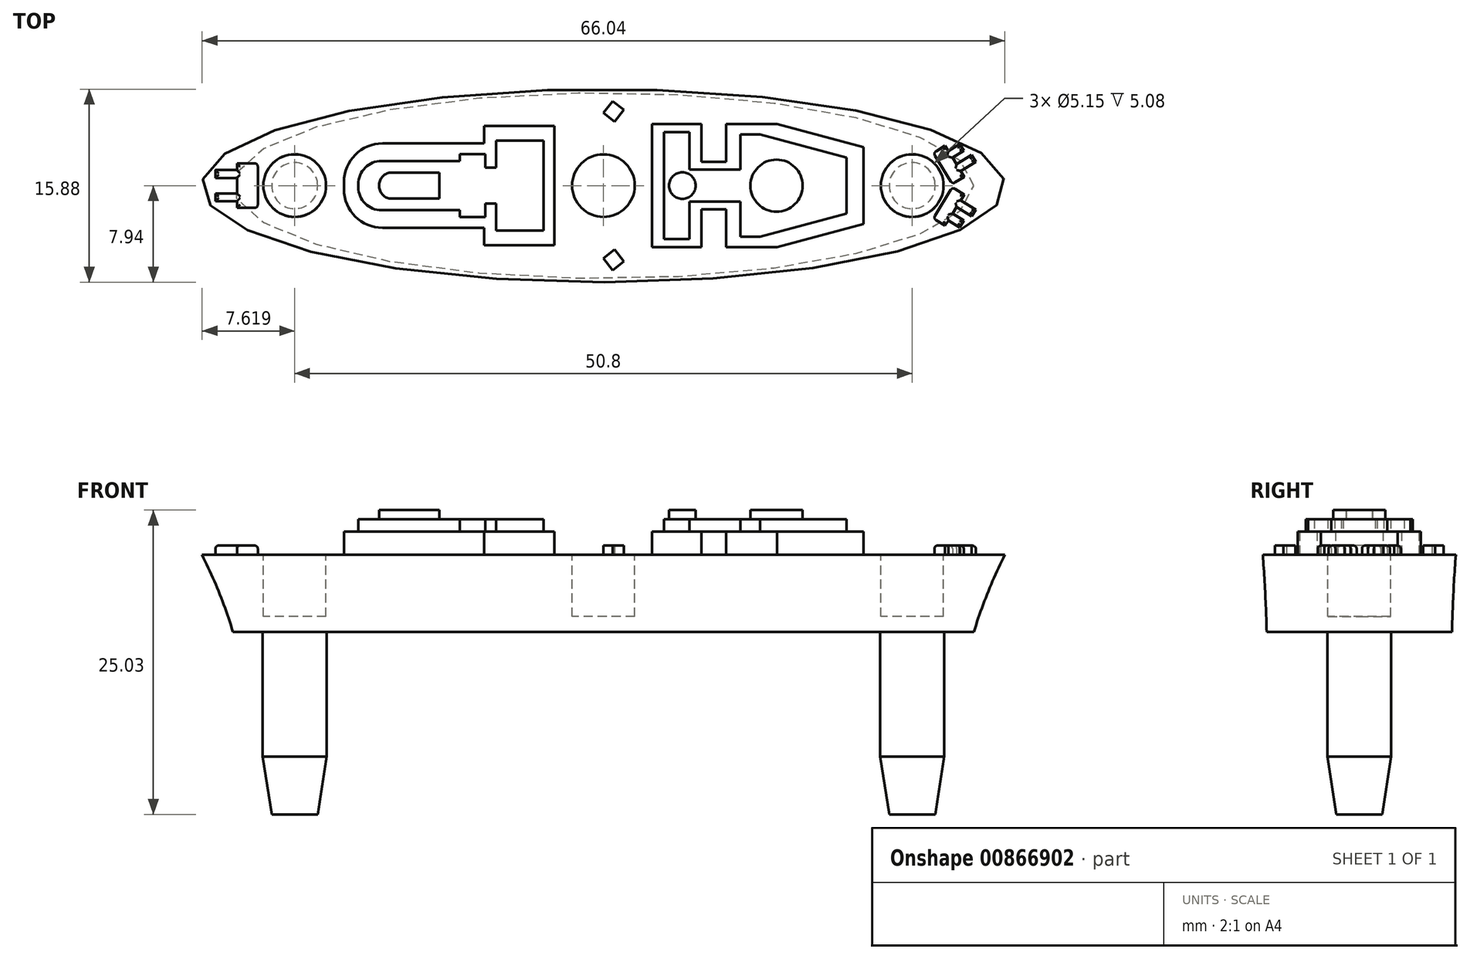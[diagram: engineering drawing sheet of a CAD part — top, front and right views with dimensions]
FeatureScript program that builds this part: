
annotation { "Feature Type Name" : "Feature", "Feature Type Description" : "" }
export const myFeature = defineFeature(function(context is Context, id is Id, definition is map)
    precondition{}
    {
        {
            var Q0;
            Q0=qCreatedBy(makeId("Top.planeOp"),FACE);
            var sketch = newSketch(context, id + "F0", { "sketchPlane" : qUnion([Q0])});
            skEllipse(sketch, "E0", {"center": v(0, 0) * mm, "majorRadius": 33.02 * mm, "minorRadius": 7.94 * mm, "majorAxis": v(1, 0)});
            skSolve(sketch);
        }
        {
            var Q0;
            Q0=qCreatedBy(makeId("Top.planeOp"),FACE);
            cPlane(context, id + "F1", {"entities" : qUnion([Q0]), "cplaneType" : CPlaneType.OFFSET, "offset" : 6.35 * mm, "oppositeDirection" : true, "width" : 152.4 * mm, "height" : 152.4 * mm});
        }
        {
            var Q0;
            Q0=qCreatedBy(id+"F1.planeOp",FACE);
            var sketch = newSketch(context, id + "F2", { "sketchPlane" : qUnion([Q0])});
            skEllipse(sketch, "E1", {"center": v(0, 0) * mm, "majorRadius": 30.48 * mm, "minorRadius": 7.62 * mm, "majorAxis": v(1, 0)});
            skSolve(sketch);
        }
        {
            var Q0;
            Q0=makeQuery(id+"F2.imprint","IMPRINT",FACE,{"disambiguationData":[TD([[makeQuery(id+"F2.imprint","IMPRINT",EDGE,{"derivedFrom":sQuery(id+"F2.wireOp",EDGE,"E1")}),1.0]])]});
            var Q1;
            Q1=makeQuery(id+"F0.imprint","IMPRINT",FACE,{"disambiguationData":[TD([[makeQuery(id+"F0.imprint","IMPRINT",EDGE,{"derivedFrom":sQuery(id+"F0.wireOp",EDGE,"E0")}),1.0]])]});
            loft(context, id + "F3", {"sheetProfilesArray" : [{ "sheetProfileEntities" : qUnion([Q0]) }, { "sheetProfileEntities" : qUnion([Q1]) }]});
        }
        {
            var Q0;
            Q0=qCreatedBy(id+"F1.planeOp",FACE);
            var sketch = newSketch(context, id + "F4", { "sketchPlane" : qUnion([Q0])});
            skLineSegment(sketch, "E2", {"start": v(-25.4, 0) * mm, "end": v(0, 0) * mm, "construction": true});
            skLineSegment(sketch, "E3", {"start": v(0, 0) * mm, "end": v(25.4, 0) * mm, "construction": true});
            skCircle(sketch, "E4", {"center": v(-25.4, 0) * mm, "radius": 2.62 * mm});
            skCircle(sketch, "E5", {"center": v(0, 0) * mm, "radius": 2.62 * mm});
            skCircle(sketch, "E6", {"center": v(25.4, 0) * mm, "radius": 2.62 * mm});
            skSolve(sketch);
        }
        {
            var Q0;
            Q0=makeQuery(id+"F3.opLoft","CAP_FACE",FACE,{"disambiguationData":[OSD([makeQuery(id+"F0.imprint","IMPRINT",FACE,{"disambiguationData":[TD([[makeQuery(id+"F0.imprint","IMPRINT",EDGE,{"derivedFrom":sQuery(id+"F0.wireOp",EDGE,"E0")}),1.0]])]})])],"isStart":true});
            var sketch = newSketch(context, id + "F5", { "sketchPlane" : qUnion([Q0])});
            skLineSegment(sketch, "E7", {"start": v(-25.4, 0) * mm, "end": v(0, 0) * mm, "construction": true});
            skLineSegment(sketch, "E8", {"start": v(0, 0) * mm, "end": v(25.4, 0) * mm, "construction": true});
            skCircle(sketch, "E9", {"center": v(-25.4, 0) * mm, "radius": 2.58 * mm});
            skCircle(sketch, "E10", {"center": v(0, 0) * mm, "radius": 2.58 * mm});
            skCircle(sketch, "E11", {"center": v(25.4, 0) * mm, "radius": 2.58 * mm});
            skSolve(sketch);
        }
        {
            var Q0;
            Q0=makeQuery(id+"F4.imprint","IMPRINT",FACE,{"disambiguationData":[TD([[makeQuery(id+"F4.imprint","IMPRINT",EDGE,{"derivedFrom":sQuery(id+"F4.wireOp",EDGE,"E4")}),1.0]])]});
            var Q1;
            Q1=makeQuery(id+"F4.imprint","IMPRINT",FACE,{"disambiguationData":[TD([[makeQuery(id+"F4.imprint","IMPRINT",EDGE,{"derivedFrom":sQuery(id+"F4.wireOp",EDGE,"E6")}),1.0]])]});
            extrude(context, id + "F6", {"entities" : qUnion([Q0, Q1]), "operationType" : NewBodyOperationType.ADD, "oppositeDirection" : true, "depth" : 15 * mm, "offsetDistance" : 25.4 * mm});
        }
        {
            var Q0;
            Q0=makeQuery(id+"F6.opExtrude","CAP_EDGE",EDGE,{"disambiguationData":[OSD([sQuery(id+"F4.wireOp",EDGE,"E4")])],"isStart":false});
            var Q1;
            Q1=makeQuery(id+"F6.opExtrude","CAP_EDGE",EDGE,{"disambiguationData":[OSD([sQuery(id+"F4.wireOp",EDGE,"E6")])],"isStart":false});
            chamfer(context, id + "F7", {"entities" : qUnion([Q0, Q1]), "chamferType" : ChamferType.TWO_OFFSETS, "width1" : 4.76 * mm, "oppositeDirection" : false, "width2" : 0.73 * mm, "tangentPropagation" : true});
        }
        {
            var Q0;
            Q0=makeQuery(id+"F5.imprint","IMPRINT",FACE,{"disambiguationData":[TD([[makeQuery(id+"F5.imprint","IMPRINT",EDGE,{"derivedFrom":sQuery(id+"F5.wireOp",EDGE,"E9")}),1.0]])]});
            var Q1;
            Q1=makeQuery(id+"F5.imprint","IMPRINT",FACE,{"disambiguationData":[TD([[makeQuery(id+"F5.imprint","IMPRINT",EDGE,{"derivedFrom":sQuery(id+"F5.wireOp",EDGE,"E10")}),1.0]])]});
            var Q2;
            Q2=makeQuery(id+"F5.imprint","IMPRINT",FACE,{"disambiguationData":[TD([[makeQuery(id+"F5.imprint","IMPRINT",EDGE,{"derivedFrom":sQuery(id+"F5.wireOp",EDGE,"E11")}),1.0]])]});
            extrude(context, id + "F8", {"entities" : qUnion([Q0, Q1, Q2]), "operationType" : NewBodyOperationType.REMOVE, "oppositeDirection" : true, "depth" : 5.08 * mm, "offsetDistance" : 25.4 * mm});
        }
        {
            var Q0;
            Q0=makeQuery(id+"F3.opLoft","CAP_FACE",FACE,{"disambiguationData":[OSD([makeQuery(id+"F0.imprint","IMPRINT",FACE,{"disambiguationData":[TD([[makeQuery(id+"F0.imprint","IMPRINT",EDGE,{"derivedFrom":sQuery(id+"F0.wireOp",EDGE,"E0")}),1.0]])]})])],"isStart":true});
            var sketch = newSketch(context, id + "F9", { "sketchPlane" : qUnion([Q0])});
            skLineSegment(sketch, "E12", {"start": v(-35.95, 0) * mm, "end": v(37.06, 0) * mm, "construction": true});
            skSolve(sketch);
        }
        {
            var Q0;
            Q0=makeQuery(id+"F9.imprint","IMPRINT",FACE,{"disambiguationData":[TD([[makeQuery(id+"F9.imprint","IMPRINT",EDGE,{"derivedFrom":makeQuery(id+"F3.opLoft","MID_CAP_EDGE",EDGE,{"disambiguationData":[OSD([sQuery(id+"F0.wireOp",EDGE,"E0")])],"capPos":1.0})}),1.0]])]});
            var sketch = newSketch(context, id + "F10", { "sketchPlane" : qUnion([Q0])});
            skLineSegment(sketch, "E13.bottom", {"start": v(-4.04, 4.91) * mm, "end": v(-9.81, 4.91) * mm});
            skLineSegment(sketch, "E13.top", {"start": v(-4.04, -4.91) * mm, "end": v(-9.81, -4.91) * mm});
            skLineSegment(sketch, "E13.left", {"start": v(-4.04, 4.91) * mm, "end": v(-4.04, -4.91) * mm});
            skLineSegment(sketch, "E13.right", {"start": v(-9.81, 4.91) * mm, "end": v(-9.81, 3.47) * mm});
            skPoint(sketch, "E13.middle", {"position": v(-6.93, 0) * mm});
            skLineSegment(sketch, "E14.bottom", {"start": v(-9.81, 3.47) * mm, "end": v(-18.17, 3.47) * mm});
            skLineSegment(sketch, "E14.top", {"start": v(-9.81, -3.47) * mm, "end": v(-18.17, -3.47) * mm});
            skLineSegment(sketch, "E14.right", {"start": v(-21.35, 0.3) * mm, "end": v(-21.35, -0.3) * mm});
            skPoint(sketch, "E14.middle", {"position": v(-15.58, 0) * mm});
            skPoint(sketch, "E15.visualSharp", {"position": v(-21.35, 3.47) * mm});
            skArc(sketch, "E15.filletArc", {"start": v(-18.17, 3.47) * mm, "mid": v(-20.42, 2.54) * mm, "end": v(-21.35, 0.3) * mm});
            skPoint(sketch, "E16.visualSharp", {"position": v(-21.35, -3.47) * mm});
            skArc(sketch, "E16.filletArc", {"start": v(-21.35, -0.3) * mm, "mid": v(-20.42, -2.54) * mm, "end": v(-18.17, -3.47) * mm});
            skLineSegment(sketch, "E17.trimOffspring", {"start": v(-9.81, -3.47) * mm, "end": v(-9.81, -4.91) * mm});
            skLineSegment(sketch, "E18.bottom", {"start": v(3.99, 5.06) * mm, "end": v(8.05, 5.06) * mm});
            skLineSegment(sketch, "E18.top", {"start": v(3.99, -5.06) * mm, "end": v(8.05, -5.06) * mm});
            skLineSegment(sketch, "E18.left", {"start": v(3.99, 5.06) * mm, "end": v(3.99, -5.06) * mm});
            skLineSegment(sketch, "E18.right", {"start": v(8.05, 5.06) * mm, "end": v(8.05, 1.95) * mm});
            skPoint(sketch, "E18.middle", {"position": v(6.02, 0) * mm});
            skLineSegment(sketch, "E19.bottom", {"start": v(8.05, 1.95) * mm, "end": v(10.08, 1.95) * mm});
            skLineSegment(sketch, "E19.top", {"start": v(8.05, -1.95) * mm, "end": v(10.08, -1.95) * mm});
            skPoint(sketch, "E19.middle", {"position": v(9.07, 0) * mm});
            skLineSegment(sketch, "E20.bottom", {"start": v(10.08, 5.06) * mm, "end": v(21.39, 5.06) * mm});
            skLineSegment(sketch, "E20.top", {"start": v(10.08, -5.06) * mm, "end": v(21.39, -5.06) * mm});
            skLineSegment(sketch, "E20.left", {"start": v(10.08, 5.06) * mm, "end": v(10.08, 1.95) * mm});
            skLineSegment(sketch, "E20.right", {"start": v(21.39, 5.06) * mm, "end": v(21.39, -5.06) * mm});
            skPoint(sketch, "E20.middle", {"position": v(15.74, 0) * mm});
            skLineSegment(sketch, "E21.trimOffspring", {"start": v(10.08, -1.95) * mm, "end": v(10.08, -5.06) * mm});
            skLineSegment(sketch, "E22.trimOffspring", {"start": v(8.05, -1.95) * mm, "end": v(8.05, -5.06) * mm});
            skSolve(sketch);
        }
        {
            var Q0;
            Q0 = qSketchRegion(id + "F10", true);
            extrude(context, id + "F11", {"entities" : qUnion([Q0]), "operationType" : NewBodyOperationType.ADD, "depth" : 1.9 * mm, "offsetDistance" : 25.4 * mm});
        }
        {
            var Q0;
            Q0=makeQuery(id+"F11.opExtrude","SWEPT_EDGE",EDGE,{"disambiguationData":[OSD([sQuery(id+"F10.wireOp",EDGE,"E20.top"),sQuery(id+"F10.wireOp",EDGE,"E20.right")])]});
            var Q1;
            Q1=makeQuery(id+"F11.opExtrude","SWEPT_EDGE",EDGE,{"disambiguationData":[OSD([sQuery(id+"F10.wireOp",EDGE,"E20.bottom"),sQuery(id+"F10.wireOp",EDGE,"E20.right")])]});
            chamfer(context, id + "F12", {"entities" : qUnion([Q0, Q1]), "chamferType" : ChamferType.OFFSET_ANGLE, "width" : 1.9 * mm, "oppositeDirection" : false, "angle" : 75 * degree, "tangentPropagation" : true});
        }
        {
            var Q0;
            Q0=makeQuery(id+"F11.opExtrude","CAP_FACE",FACE,{"disambiguationData":[OSD([sQuery(id+"F10.wireOp",EDGE,"E13.bottom"),sQuery(id+"F10.wireOp",EDGE,"E13.top"),sQuery(id+"F10.wireOp",EDGE,"E13.left"),sQuery(id+"F10.wireOp",EDGE,"E13.right"),sQuery(id+"F10.wireOp",EDGE,"E14.bottom"),sQuery(id+"F10.wireOp",EDGE,"E14.top"),sQuery(id+"F10.wireOp",EDGE,"E14.right"),sQuery(id+"F10.wireOp",EDGE,"E15.filletArc"),sQuery(id+"F10.wireOp",EDGE,"E16.filletArc"),sQuery(id+"F10.wireOp",EDGE,"E17.trimOffspring")])],"isStart":false});
            var sketch = newSketch(context, id + "F13", { "sketchPlane" : qUnion([Q0])});
            skLineSegment(sketch, "E23.bottom", {"start": v(-4.93, 3.7) * mm, "end": v(-8.82, 3.7) * mm});
            skLineSegment(sketch, "E23.top", {"start": v(-4.93, -3.7) * mm, "end": v(-8.82, -3.7) * mm});
            skLineSegment(sketch, "E23.left", {"start": v(-4.93, 3.7) * mm, "end": v(-4.93, -3.7) * mm});
            skLineSegment(sketch, "E23.right", {"start": v(-8.82, 3.7) * mm, "end": v(-8.82, 1.48) * mm});
            skPoint(sketch, "E23.middle", {"position": v(-6.87, 0) * mm});
            skLineSegment(sketch, "E24.bottom", {"start": v(-8.82, 1.48) * mm, "end": v(-9.72, 1.48) * mm});
            skLineSegment(sketch, "E24.top", {"start": v(-8.82, -1.48) * mm, "end": v(-9.72, -1.48) * mm});
            skPoint(sketch, "E25", {"position": v(-8.82, 0) * mm});
            skLineSegment(sketch, "E26.bottom", {"start": v(-9.72, 2.6) * mm, "end": v(-11.8, 2.6) * mm});
            skLineSegment(sketch, "E26.top", {"start": v(-9.72, -2.6) * mm, "end": v(-11.8, -2.6) * mm});
            skLineSegment(sketch, "E26.left", {"start": v(-9.72, 2.6) * mm, "end": v(-9.72, 1.48) * mm});
            skLineSegment(sketch, "E26.right", {"start": v(-11.8, 2.6) * mm, "end": v(-11.8, 2.03) * mm});
            skPoint(sketch, "E26.middle", {"position": v(-10.76, 0) * mm});
            skLineSegment(sketch, "E27.bottom", {"start": v(-11.8, 2.03) * mm, "end": v(-18.26, 2.03) * mm});
            skLineSegment(sketch, "E27.top", {"start": v(-11.8, -2.03) * mm, "end": v(-18.26, -2.03) * mm});
            skLineSegment(sketch, "E27.right", {"start": v(-20.16, 0.12) * mm, "end": v(-20.16, -0.12) * mm});
            skPoint(sketch, "E27.middle", {"position": v(-15.98, 0) * mm});
            skLineSegment(sketch, "E28.trimOffspring", {"start": v(-11.8, -2.03) * mm, "end": v(-11.8, -2.6) * mm});
            skLineSegment(sketch, "E29.trimOffspring", {"start": v(-8.82, -1.48) * mm, "end": v(-8.82, -3.7) * mm});
            skLineSegment(sketch, "E30.trimOffspring", {"start": v(-9.72, -1.48) * mm, "end": v(-9.72, -2.6) * mm});
            skPoint(sketch, "E31.visualSharp", {"position": v(-20.16, 2.03) * mm});
            skArc(sketch, "E31.filletArc", {"start": v(-18.26, 2.03) * mm, "mid": v(-19.6, 1.47) * mm, "end": v(-20.16, 0.12) * mm});
            skPoint(sketch, "E32.visualSharp", {"position": v(-20.16, -2.03) * mm});
            skArc(sketch, "E32.filletArc", {"start": v(-20.16, -0.12) * mm, "mid": v(-19.6, -1.47) * mm, "end": v(-18.26, -2.03) * mm});
            skLineSegment(sketch, "E33.bottom", {"start": v(4.99, 4.39) * mm, "end": v(7.08, 4.39) * mm});
            skLineSegment(sketch, "E33.top", {"start": v(4.99, -4.39) * mm, "end": v(7.08, -4.39) * mm});
            skLineSegment(sketch, "E33.left", {"start": v(4.99, 4.39) * mm, "end": v(4.99, -4.39) * mm});
            skLineSegment(sketch, "E33.right", {"start": v(7.08, 4.39) * mm, "end": v(7.08, 1.3) * mm});
            skPoint(sketch, "E33.middle", {"position": v(6.03, 0) * mm});
            skLineSegment(sketch, "E34.bottom", {"start": v(11.26, 4.2) * mm, "end": v(20, 4.2) * mm});
            skLineSegment(sketch, "E34.top", {"start": v(11.26, -4.2) * mm, "end": v(20, -4.2) * mm});
            skLineSegment(sketch, "E34.left", {"start": v(11.26, 4.2) * mm, "end": v(11.26, 1.3) * mm});
            skLineSegment(sketch, "E34.right", {"start": v(20, 4.2) * mm, "end": v(20, -4.2) * mm});
            skLineSegment(sketch, "E35.bottom", {"start": v(7.08, 1.3) * mm, "end": v(11.26, 1.3) * mm});
            skLineSegment(sketch, "E35.top", {"start": v(7.08, -1.3) * mm, "end": v(11.26, -1.3) * mm});
            skLineSegment(sketch, "E36.trimOffspring", {"start": v(11.26, -1.3) * mm, "end": v(11.26, -4.2) * mm});
            skLineSegment(sketch, "E37.trimOffspring", {"start": v(7.08, -1.3) * mm, "end": v(7.08, -4.39) * mm});
            skSolve(sketch);
        }
        {
            var Q0;
            Q0 = qSketchRegion(id + "F13", true);
            extrude(context, id + "F14", {"entities" : qUnion([Q0]), "operationType" : NewBodyOperationType.ADD, "depth" : 1.02 * mm, "offsetDistance" : 25.4 * mm});
        }
        {
            var Q0;
            Q0=makeQuery(id+"F14.opExtrude","SWEPT_EDGE",EDGE,{"disambiguationData":[OSD([sQuery(id+"F13.wireOp",EDGE,"E34.top"),sQuery(id+"F13.wireOp",EDGE,"E34.right")])]});
            var Q1;
            Q1=makeQuery(id+"F14.opExtrude","SWEPT_EDGE",EDGE,{"disambiguationData":[OSD([sQuery(id+"F13.wireOp",EDGE,"E34.bottom"),sQuery(id+"F13.wireOp",EDGE,"E34.right")])]});
            chamfer(context, id + "F15", {"entities" : qUnion([Q0, Q1]), "chamferType" : ChamferType.OFFSET_ANGLE, "width" : 1.9 * mm, "oppositeDirection" : false, "angle" : 75 * degree, "tangentPropagation" : true});
        }
        {
            var Q0;
            Q0=makeQuery(id+"F14.opExtrude","CAP_FACE",FACE,{"disambiguationData":[OSD([sQuery(id+"F13.wireOp",EDGE,"E23.bottom"),sQuery(id+"F13.wireOp",EDGE,"E23.top"),sQuery(id+"F13.wireOp",EDGE,"E23.left"),sQuery(id+"F13.wireOp",EDGE,"E23.right"),sQuery(id+"F13.wireOp",EDGE,"E24.bottom"),sQuery(id+"F13.wireOp",EDGE,"E24.top"),sQuery(id+"F13.wireOp",EDGE,"E26.bottom"),sQuery(id+"F13.wireOp",EDGE,"E26.top"),sQuery(id+"F13.wireOp",EDGE,"E26.left"),sQuery(id+"F13.wireOp",EDGE,"E26.right"),sQuery(id+"F13.wireOp",EDGE,"E27.bottom"),sQuery(id+"F13.wireOp",EDGE,"E27.top"),sQuery(id+"F13.wireOp",EDGE,"E27.right"),sQuery(id+"F13.wireOp",EDGE,"E28.trimOffspring"),sQuery(id+"F13.wireOp",EDGE,"E29.trimOffspring"),sQuery(id+"F13.wireOp",EDGE,"E30.trimOffspring"),sQuery(id+"F13.wireOp",EDGE,"E31.filletArc"),sQuery(id+"F13.wireOp",EDGE,"E32.filletArc")])],"isStart":false});
            var sketch = newSketch(context, id + "F16", { "sketchPlane" : qUnion([Q0])});
            skLineSegment(sketch, "E38.bottom", {"start": v(-13.51, 1.08) * mm, "end": v(-17.43, 1.08) * mm});
            skLineSegment(sketch, "E38.top", {"start": v(-13.51, -1.08) * mm, "end": v(-17.43, -1.08) * mm});
            skLineSegment(sketch, "E38.left", {"start": v(-13.51, 1.08) * mm, "end": v(-13.51, -1.08) * mm});
            skLineSegment(sketch, "E38.right", {"start": v(-18.44, 0.06) * mm, "end": v(-18.44, -0.06) * mm});
            skPoint(sketch, "E38.middle", {"position": v(-15.98, 0) * mm});
            skCircle(sketch, "E39", {"center": v(6.5, 0) * mm, "radius": 1.1 * mm});
            skCircle(sketch, "E40", {"center": v(14.24, 0) * mm, "radius": 2.14 * mm});
            skPoint(sketch, "E41.visualSharp", {"position": v(-18.44, 1.08) * mm});
            skArc(sketch, "E41.filletArc", {"start": v(-17.43, 1.08) * mm, "mid": v(-18.14, 0.78) * mm, "end": v(-18.44, 0.06) * mm});
            skPoint(sketch, "E42.visualSharp", {"position": v(-18.44, -1.08) * mm});
            skArc(sketch, "E42.filletArc", {"start": v(-18.44, -0.06) * mm, "mid": v(-18.14, -0.78) * mm, "end": v(-17.43, -1.08) * mm});
            skSolve(sketch);
        }
        {
            var Q0;
            Q0 = qSketchRegion(id + "F16", true);
            extrude(context, id + "F17", {"entities" : qUnion([Q0]), "operationType" : NewBodyOperationType.ADD, "depth" : 0.76 * mm, "offsetDistance" : 25.4 * mm});
        }
        {
            var Q0;
            Q0=makeQuery(id+"F9.imprint","IMPRINT",FACE,{"disambiguationData":[TD([[makeQuery(id+"F9.imprint","IMPRINT",EDGE,{"derivedFrom":makeQuery(id+"F3.opLoft","MID_CAP_EDGE",EDGE,{"disambiguationData":[OSD([sQuery(id+"F0.wireOp",EDGE,"E0")])],"capPos":1.0})}),1.0]])]});
            var sketch = newSketch(context, id + "F18", { "sketchPlane" : qUnion([Q0])});
            skLineSegment(sketch, "E43.bottom", {"start": v(-28.44, 1.83) * mm, "end": v(-30.15, 1.83) * mm});
            skLineSegment(sketch, "E43.top", {"start": v(-28.44, -1.83) * mm, "end": v(-30.15, -1.83) * mm});
            skLineSegment(sketch, "E43.left", {"start": v(-28.44, 1.83) * mm, "end": v(-28.44, -1.83) * mm});
            skLineSegment(sketch, "E43.right", {"start": v(-30.15, 1.83) * mm, "end": v(-30.15, 1.28) * mm});
            skPoint(sketch, "E43.middle", {"position": v(-29.3, 0) * mm});
            skLineSegment(sketch, "E44.bottom", {"start": v(-30.15, 0.64) * mm, "end": v(-31.92, 0.64) * mm});
            skLineSegment(sketch, "E44.top", {"start": v(-30.15, 1.28) * mm, "end": v(-31.92, 1.28) * mm});
            skLineSegment(sketch, "E44.right", {"start": v(-31.92, 0.64) * mm, "end": v(-31.92, 1.28) * mm});
            skLineSegment(sketch, "E45.MirrorCS", {"start": v(-30.15, -0.64) * mm, "end": v(-31.92, -0.64) * mm});
            skLineSegment(sketch, "E46.MirrorCS", {"start": v(-30.15, -1.28) * mm, "end": v(-31.92, -1.28) * mm});
            skLineSegment(sketch, "E47.MirrorCS", {"start": v(-31.92, -0.64) * mm, "end": v(-31.92, -1.28) * mm});
            skLineSegment(sketch, "E48.trimOffspring", {"start": v(-30.15, -1.28) * mm, "end": v(-30.15, -1.83) * mm});
            skLineSegment(sketch, "E49.trimOffspring", {"start": v(-30.15, 0.64) * mm, "end": v(-30.15, -0.64) * mm});
            skLineSegment(sketch, "E50", {"start": v(0.77, 6.95) * mm, "end": v(0, 5.98) * mm});
            skLineSegment(sketch, "E51", {"start": v(0, 5.98) * mm, "end": v(0.91, 5.26) * mm});
            skLineSegment(sketch, "E52", {"start": v(0.91, 5.26) * mm, "end": v(1.69, 6.23) * mm});
            skLineSegment(sketch, "E53", {"start": v(1.69, 6.23) * mm, "end": v(0.77, 6.95) * mm});
            skLineSegment(sketch, "E54.MirrorCS", {"start": v(0.77, -6.95) * mm, "end": v(0, -5.98) * mm});
            skLineSegment(sketch, "E55.MirrorCS", {"start": v(0.91, -5.26) * mm, "end": v(1.69, -6.23) * mm});
            skLineSegment(sketch, "E56.MirrorCS", {"start": v(1.69, -6.23) * mm, "end": v(0.77, -6.95) * mm});
            skLineSegment(sketch, "E57.MirrorCS", {"start": v(0, -5.98) * mm, "end": v(0.91, -5.26) * mm});
            skLineSegment(sketch, "E58", {"start": v(27.13, 2.69) * mm, "end": v(28.71, 0.13) * mm});
            skLineSegment(sketch, "E59", {"start": v(28.71, 0.13) * mm, "end": v(29.69, 0.73) * mm});
            skLineSegment(sketch, "E60", {"start": v(29.69, 0.73) * mm, "end": v(29.4, 1.2) * mm});
            skLineSegment(sketch, "E61", {"start": v(28.1, 3.3) * mm, "end": v(27.13, 2.69) * mm});
            skLineSegment(sketch, "E62", {"start": v(29.05, 1.76) * mm, "end": v(30.29, 2.53) * mm});
            skLineSegment(sketch, "E63", {"start": v(30.29, 2.53) * mm, "end": v(30.63, 1.97) * mm});
            skLineSegment(sketch, "E64", {"start": v(30.63, 1.97) * mm, "end": v(29.4, 1.2) * mm});
            skLineSegment(sketch, "E65", {"start": v(28.72, 2.3) * mm, "end": v(29.64, 2.87) * mm});
            skLineSegment(sketch, "E66", {"start": v(29.64, 2.87) * mm, "end": v(29.3, 3.43) * mm});
            skLineSegment(sketch, "E67", {"start": v(29.3, 3.43) * mm, "end": v(28.37, 2.86) * mm});
            skLineSegment(sketch, "E68.trimOffspring", {"start": v(28.37, 2.86) * mm, "end": v(28.1, 3.3) * mm});
            skLineSegment(sketch, "E69.trimOffspring", {"start": v(29.05, 1.76) * mm, "end": v(28.72, 2.3) * mm});
            skLineSegment(sketch, "E70.MirrorCS", {"start": v(28.37, -2.86) * mm, "end": v(28.1, -3.3) * mm});
            skLineSegment(sketch, "E71.MirrorCS", {"start": v(30.29, -2.53) * mm, "end": v(30.63, -1.97) * mm});
            skLineSegment(sketch, "E72.MirrorCS", {"start": v(29.69, -0.73) * mm, "end": v(29.4, -1.2) * mm});
            skLineSegment(sketch, "E73.MirrorCS", {"start": v(29.05, -1.76) * mm, "end": v(28.72, -2.3) * mm});
            skLineSegment(sketch, "E74.MirrorCS", {"start": v(29.64, -2.87) * mm, "end": v(29.3, -3.43) * mm});
            skLineSegment(sketch, "E75.MirrorCS", {"start": v(28.72, -2.3) * mm, "end": v(29.64, -2.87) * mm});
            skLineSegment(sketch, "E76.MirrorCS", {"start": v(29.05, -1.76) * mm, "end": v(30.29, -2.53) * mm});
            skLineSegment(sketch, "E77.MirrorCS", {"start": v(28.1, -3.3) * mm, "end": v(27.13, -2.69) * mm});
            skLineSegment(sketch, "E78.MirrorCS", {"start": v(29.3, -3.43) * mm, "end": v(28.37, -2.86) * mm});
            skLineSegment(sketch, "E79.MirrorCS", {"start": v(30.63, -1.97) * mm, "end": v(29.4, -1.2) * mm});
            skLineSegment(sketch, "E80.MirrorCS", {"start": v(27.13, -2.69) * mm, "end": v(28.71, -0.13) * mm});
            skLineSegment(sketch, "E81.MirrorCS", {"start": v(28.71, -0.13) * mm, "end": v(29.69, -0.73) * mm});
            skSolve(sketch);
        }
        {
            var Q0;
            Q0 = qSketchRegion(id + "F18", true);
            extrude(context, id + "F19", {"entities" : qUnion([Q0]), "operationType" : NewBodyOperationType.ADD, "depth" : 0.76 * mm, "offsetDistance" : 25.4 * mm});
        }
        {
            var Q0;
            Q0=makeQuery(id+"F19.opExtrude","CAP_FACE",FACE,{"disambiguationData":[OSD([sQuery(id+"F18.wireOp",EDGE,"E58"),sQuery(id+"F18.wireOp",EDGE,"E59"),sQuery(id+"F18.wireOp",EDGE,"E60"),sQuery(id+"F18.wireOp",EDGE,"E61"),sQuery(id+"F18.wireOp",EDGE,"E62"),sQuery(id+"F18.wireOp",EDGE,"E63"),sQuery(id+"F18.wireOp",EDGE,"E64"),sQuery(id+"F18.wireOp",EDGE,"E65"),sQuery(id+"F18.wireOp",EDGE,"E66"),sQuery(id+"F18.wireOp",EDGE,"E67"),sQuery(id+"F18.wireOp",EDGE,"E68.trimOffspring"),sQuery(id+"F18.wireOp",EDGE,"E69.trimOffspring")])],"isStart":false});
            var Q1;
            Q1=makeQuery(id+"F19.opExtrude","CAP_FACE",FACE,{"disambiguationData":[OSD([sQuery(id+"F18.wireOp",EDGE,"E70.MirrorCS"),sQuery(id+"F18.wireOp",EDGE,"E71.MirrorCS"),sQuery(id+"F18.wireOp",EDGE,"E72.MirrorCS"),sQuery(id+"F18.wireOp",EDGE,"E73.MirrorCS"),sQuery(id+"F18.wireOp",EDGE,"E74.MirrorCS"),sQuery(id+"F18.wireOp",EDGE,"E75.MirrorCS"),sQuery(id+"F18.wireOp",EDGE,"E76.MirrorCS"),sQuery(id+"F18.wireOp",EDGE,"E77.MirrorCS"),sQuery(id+"F18.wireOp",EDGE,"E78.MirrorCS"),sQuery(id+"F18.wireOp",EDGE,"E79.MirrorCS"),sQuery(id+"F18.wireOp",EDGE,"E80.MirrorCS"),sQuery(id+"F18.wireOp",EDGE,"E81.MirrorCS")])],"isStart":false});
            var Q2;
            Q2=makeQuery(id+"F19.opExtrude","CAP_FACE",FACE,{"disambiguationData":[OSD([sQuery(id+"F18.wireOp",EDGE,"E43.bottom"),sQuery(id+"F18.wireOp",EDGE,"E43.top"),sQuery(id+"F18.wireOp",EDGE,"E43.left"),sQuery(id+"F18.wireOp",EDGE,"E43.right"),sQuery(id+"F18.wireOp",EDGE,"E44.bottom"),sQuery(id+"F18.wireOp",EDGE,"E44.top"),sQuery(id+"F18.wireOp",EDGE,"E44.right"),sQuery(id+"F18.wireOp",EDGE,"E45.MirrorCS"),sQuery(id+"F18.wireOp",EDGE,"E46.MirrorCS"),sQuery(id+"F18.wireOp",EDGE,"E47.MirrorCS"),sQuery(id+"F18.wireOp",EDGE,"E48.trimOffspring"),sQuery(id+"F18.wireOp",EDGE,"E49.trimOffspring")])],"isStart":false});
            var Q3;
            Q3=makeQuery(id+"F19.opExtrude","SWEPT_EDGE",EDGE,{"disambiguationData":[OSD([sQuery(id+"F18.wireOp",EDGE,"E43.bottom"),sQuery(id+"F18.wireOp",EDGE,"E43.left")])]});
            var Q4;
            Q4=makeQuery(id+"F19.opExtrude","SWEPT_EDGE",EDGE,{"disambiguationData":[OSD([sQuery(id+"F18.wireOp",EDGE,"E43.top"),sQuery(id+"F18.wireOp",EDGE,"E43.left")])]});
            var Q5;
            Q5=makeQuery(id+"F19.opExtrude","SWEPT_EDGE",EDGE,{"disambiguationData":[OSD([sQuery(id+"F18.wireOp",EDGE,"E80.MirrorCS"),sQuery(id+"F18.wireOp",EDGE,"E81.MirrorCS")])]});
            var Q6;
            Q6=makeQuery(id+"F19.opExtrude","SWEPT_EDGE",EDGE,{"disambiguationData":[OSD([sQuery(id+"F18.wireOp",EDGE,"E77.MirrorCS"),sQuery(id+"F18.wireOp",EDGE,"E80.MirrorCS")])]});
            var Q7;
            Q7=makeQuery(id+"F19.opExtrude","SWEPT_EDGE",EDGE,{"disambiguationData":[OSD([sQuery(id+"F18.wireOp",EDGE,"E58"),sQuery(id+"F18.wireOp",EDGE,"E61")])]});
            var Q8;
            Q8=makeQuery(id+"F19.opExtrude","SWEPT_EDGE",EDGE,{"disambiguationData":[OSD([sQuery(id+"F18.wireOp",EDGE,"E58"),sQuery(id+"F18.wireOp",EDGE,"E59")])]});
            fillet(context, id + "F20", {"entities" : qUnion([Q0, Q1, Q2, Q3, Q4, Q5, Q6, Q7, Q8]), "radius" : 0.25 * mm, "tangentPropagation" : true, "allowEdgeOverflow" : false});
        }
    });
